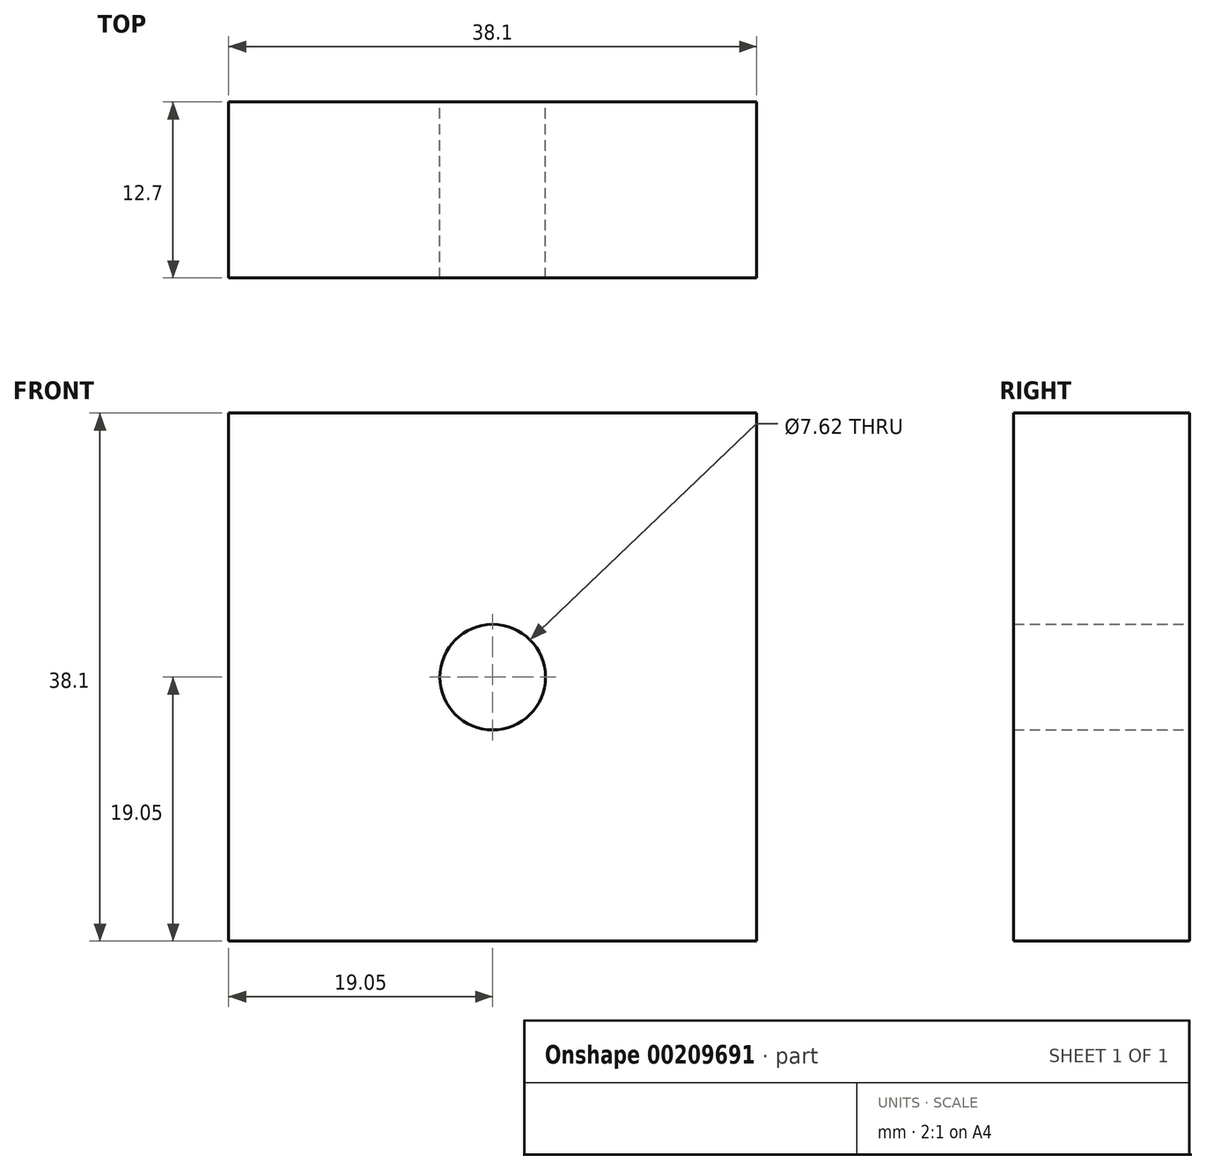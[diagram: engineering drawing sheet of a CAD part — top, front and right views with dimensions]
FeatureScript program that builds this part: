
annotation { "Feature Type Name" : "Feature", "Feature Type Description" : "" }
export const myFeature = defineFeature(function(context is Context, id is Id, definition is map)
    precondition{}
    {
        {
            var Q0;
            Q0=qCreatedBy(makeId("Front.planeOp"),FACE);
            var sketch = newSketch(context, id + "F0", { "sketchPlane" : qUnion([Q0])});
            skLineSegment(sketch, "E0.bottom", {"start": v(19.05, 19.05) * mm, "end": v(-19.05, 19.05) * mm});
            skLineSegment(sketch, "E0.top", {"start": v(19.05, -19.05) * mm, "end": v(-19.05, -19.05) * mm});
            skLineSegment(sketch, "E0.left", {"start": v(19.05, 19.05) * mm, "end": v(19.05, -19.05) * mm});
            skLineSegment(sketch, "E0.right", {"start": v(-19.05, 19.05) * mm, "end": v(-19.05, -19.05) * mm});
            skPoint(sketch, "E0.middle", {"position": v(0, 0) * mm});
            skCircle(sketch, "E1", {"center": v(0, 0) * mm, "radius": 3.81 * mm});
            skSolve(sketch);
        }
        {
            var Q0;
            Q0 = qSketchRegion(id + "F0", true);
            extrude(context, id + "F1", {"entities" : qUnion([Q0]), "depth" : 12.7 * mm});
        }
    });
